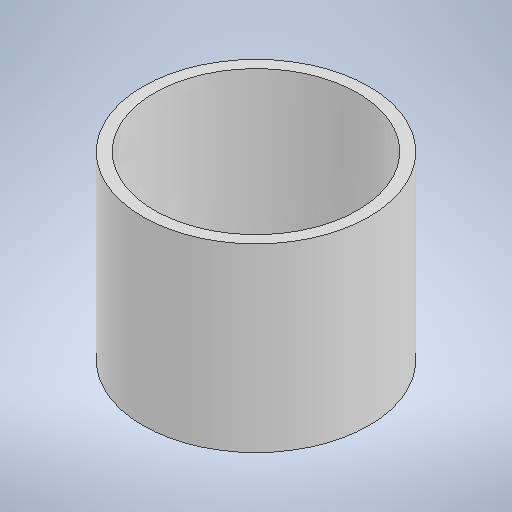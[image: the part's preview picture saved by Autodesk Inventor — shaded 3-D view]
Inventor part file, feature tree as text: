
AUTODESK INVENTOR PART (.ipt)
format: ipt  version: 2025 (Build 290162000, 162)  size: 209,920 bytes
history: native  units: mm
features: sketch x5, extrude x3, other x1
ambient origin geometry x8: Origin, YZ Plane, XZ Plane, XY Plane, X Axis, Y Axis, Z Axis, Center Point
bodies: Body1 (feature_tree)
feature tree (9):
  other  "Bryła1"
  extrude  "Wyciągnięcie proste1"  Depth=100.0mm
  extrude  "Wyciągnięcie proste2"  Depth=80.0mm TaperAngle=0.0deg
  sketch  "Szkic3"
  extrude  "Wyciągnięcie proste3"  Depth=90.0mm
  sketch  "Szkic9"
  sketch  "Szkic1"
  sketch  "Szkic2"
  sketch  "Szkic4"
